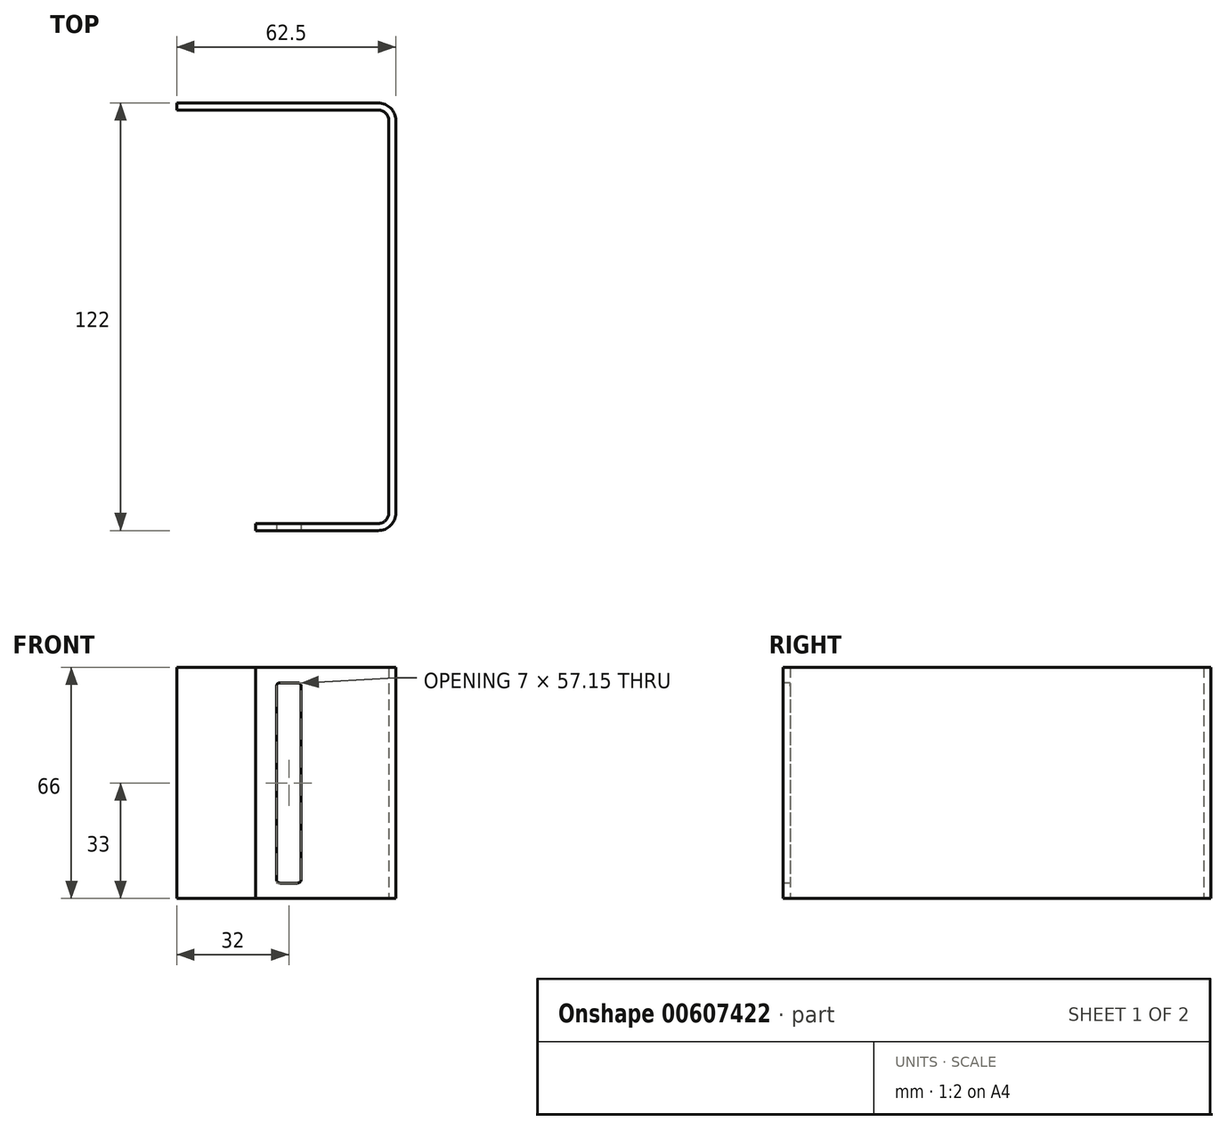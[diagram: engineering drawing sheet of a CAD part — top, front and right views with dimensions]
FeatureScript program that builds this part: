
annotation { "Feature Type Name" : "Feature", "Feature Type Description" : "" }
export const myFeature = defineFeature(function(context is Context, id is Id, definition is map)
    precondition{}
    {
        {
            var Q0;
            Q0=qCreatedBy(makeId("Top.planeOp"),FACE);
            var sketch = newSketch(context, id + "F0", { "sketchPlane" : qUnion([Q0])});
            skLineSegment(sketch, "E0", {"start": v(0, 0) * mm, "end": v(57.5, 0) * mm});
            skLineSegment(sketch, "E1", {"start": v(62.5, -5) * mm, "end": v(62.5, -117) * mm});
            skLineSegment(sketch, "E2", {"start": v(57.5, -122) * mm, "end": v(22.5, -122) * mm});
            skPoint(sketch, "E3.visualSharp", {"position": v(62.5, 0) * mm});
            skArc(sketch, "E3.filletArc", {"start": v(62.5, -5) * mm, "mid": v(61.04, -1.46) * mm, "end": v(57.5, 0) * mm});
            skPoint(sketch, "E4.visualSharp", {"position": v(62.5, -122) * mm});
            skArc(sketch, "E4.filletArc", {"start": v(57.5, -122) * mm, "mid": v(61.04, -120.54) * mm, "end": v(62.5, -117) * mm});
            skLineSegment(sketch, "E5.0", {"start": v(57.5, -120) * mm, "end": v(22.5, -120) * mm});
            skLineSegment(sketch, "E5.1", {"start": v(0, -2) * mm, "end": v(57.5, -2) * mm});
            skArc(sketch, "E5.2", {"start": v(60.5, -5) * mm, "mid": v(59.62, -2.88) * mm, "end": v(57.5, -2) * mm});
            skLineSegment(sketch, "E5.3", {"start": v(60.5, -5) * mm, "end": v(60.5, -117) * mm});
            skArc(sketch, "E5.4", {"start": v(57.5, -120) * mm, "mid": v(59.62, -119.12) * mm, "end": v(60.5, -117) * mm});
            skLineSegment(sketch, "E6", {"start": v(22.5, -122) * mm, "end": v(22.5, -120) * mm});
            skLineSegment(sketch, "E7", {"start": v(0, 0) * mm, "end": v(0, -2) * mm});
            skSolve(sketch);
        }
        {
            var Q0;
            Q0=makeQuery(id+"F0.imprint","IMPRINT",FACE,{"disambiguationData":[TD([[makeQuery(id+"F0.imprint","IMPRINT",EDGE,{"derivedFrom":sQuery(id+"F0.wireOp",EDGE,"E0")}),-1.0]])]});
            extrude(context, id + "F1", {"entities" : qUnion([Q0]), "depth" : 66 * mm, "offsetDistance" : 25 * mm});
        }
        {
            var Q0;
            Q0=makeQuery(id+"F1.opExtrude","SWEPT_FACE",FACE,{"disambiguationData":[OSD([sQuery(id+"F0.wireOp",EDGE,"E2")])]});
            var sketch = newSketch(context, id + "F2", { "sketchPlane" : qUnion([Q0])});
            skLineSegment(sketch, "E8.bottom", {"start": v(29.5, 61.57) * mm, "end": v(34.5, 61.57) * mm});
            skLineSegment(sketch, "E8.top", {"start": v(29.5, 4.42) * mm, "end": v(34.5, 4.42) * mm});
            skLineSegment(sketch, "E8.left", {"start": v(28.5, 60.57) * mm, "end": v(28.5, 5.42) * mm});
            skLineSegment(sketch, "E8.right", {"start": v(35.5, 60.57) * mm, "end": v(35.5, 5.42) * mm});
            skLineSegment(sketch, "E9", {"start": v(22.5, 33) * mm, "end": v(57.5, 33) * mm, "construction": true});
            skPoint(sketch, "E10", {"position": v(35.5, 33) * mm});
            skPoint(sketch, "E11.visualSharp", {"position": v(28.5, 61.57) * mm});
            skArc(sketch, "E11.filletArc", {"start": v(29.5, 61.57) * mm, "mid": v(28.8, 61.28) * mm, "end": v(28.5, 60.57) * mm});
            skPoint(sketch, "E12.visualSharp", {"position": v(35.5, 4.42) * mm});
            skArc(sketch, "E12.filletArc", {"start": v(34.5, 4.42) * mm, "mid": v(35.2, 4.72) * mm, "end": v(35.5, 5.42) * mm});
            skPoint(sketch, "E13.visualSharp", {"position": v(35.5, 61.57) * mm});
            skArc(sketch, "E13.filletArc", {"start": v(35.5, 60.57) * mm, "mid": v(35.2, 61.28) * mm, "end": v(34.5, 61.57) * mm});
            skPoint(sketch, "E14.visualSharp", {"position": v(28.5, 4.42) * mm});
            skArc(sketch, "E14.filletArc", {"start": v(28.5, 5.42) * mm, "mid": v(28.8, 4.72) * mm, "end": v(29.5, 4.42) * mm});
            skSolve(sketch);
        }
        {
            var Q0;
            Q0=makeQuery(id+"F2.imprint","IMPRINT",FACE,{"disambiguationData":[TD([[makeQuery(id+"F2.imprint","IMPRINT",EDGE,{"derivedFrom":sQuery(id+"F2.wireOp",EDGE,"E8.bottom")}),-1.0]])]});
            extrude(context, id + "F3", {"entities" : qUnion([Q0]), "operationType" : NewBodyOperationType.REMOVE, "oppositeDirection" : true, "depth" : 25 * mm, "offsetDistance" : 25 * mm});
        }
    });
